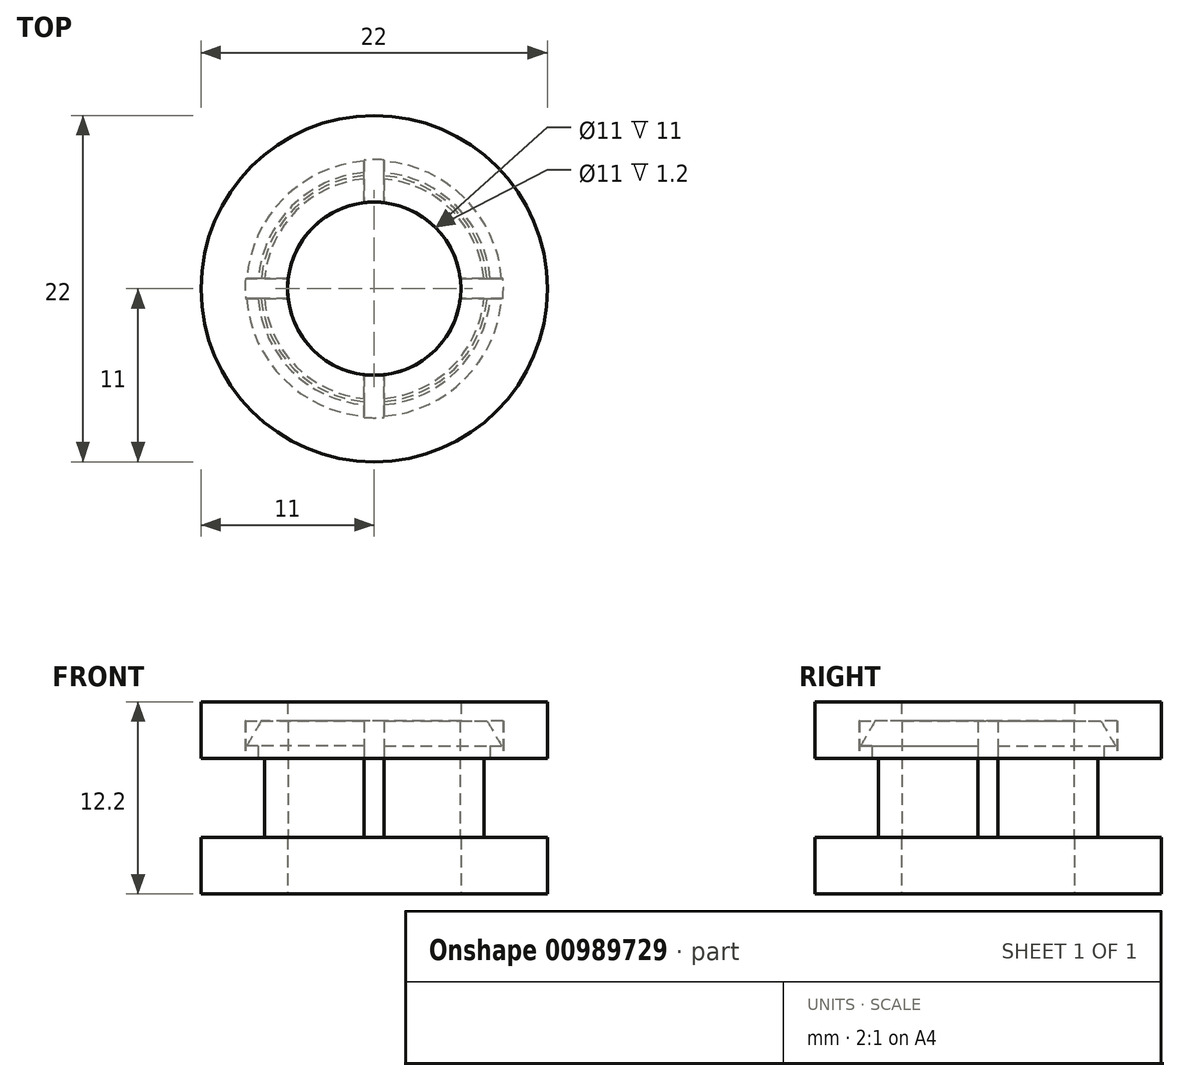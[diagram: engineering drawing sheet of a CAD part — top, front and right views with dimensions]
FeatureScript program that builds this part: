
annotation { "Feature Type Name" : "Feature", "Feature Type Description" : "" }
export const myFeature = defineFeature(function(context is Context, id is Id, definition is map)
    precondition{}
    {
        {
            assignVariable(context, id + "F0", {"name" : "WallThickness", "anyValue" : 5 * mm});
        }
        {
            assignVariable(context, id + "F1", {"name" : "WedgeLength", "anyValue" : 1.6 * mm});
        }
        {
            assignVariable(context, id + "F2", {"name" : "FlangeLength", "anyValue" : 0.8 * mm});
        }
        {
            assignVariable(context, id + "F3", {"name" : "CapThickness", "anyValue" : (getVariable(context, 'WedgeLength') + getVariable(context, 'FlangeLength')) + 1.2 * mm});
        }
        {
            var Q0;
            Q0=qCreatedBy(makeId("Top.planeOp"),FACE);
            var sketch = newSketch(context, id + "F4", { "sketchPlane" : qUnion([Q0])});
            skCircle(sketch, "E0", {"center": v(0, 0) * mm, "radius": 5.5 * mm});
            skCircle(sketch, "E1", {"center": v(0, 0) * mm, "radius": 7 * mm});
            skCircle(sketch, "E2", {"center": v(0, 0) * mm, "radius": 11 * mm});
            skCircle(sketch, "E3", {"center": v(0, 0) * mm, "radius": 8.2 * mm});
            skCircle(sketch, "E4", {"center": v(0, 0) * mm, "radius": 7.4 * mm});
            skLineSegment(sketch, "E5", {"start": v(0.64, -13.57) * mm, "end": v(0.64, 0) * mm});
            skLineSegment(sketch, "E6.MirrorCS", {"start": v(-0.64, -13.57) * mm, "end": v(-0.64, 0) * mm});
            skSolve(sketch);
        }
        {
            var Q0;
            Q0=qCreatedBy(makeId("Front.planeOp"),FACE);
            var sketch = newSketch(context, id + "F5", { "sketchPlane" : qUnion([Q0])});
            skLineSegment(sketch, "E7", {"start": v(0, 0) * mm, "end": v(0, 32.73) * mm, "construction": true});
            skSolve(sketch);
        }
        {
            var Q0;
            Q0=makeQuery(id+"F4.imprint","IMPRINT",FACE,{"disambiguationData":[TD([[makeQuery(id+"F4.imprint","IMPRINT",EDGE,{"derivedFrom":sQuery(id+"F4.wireOp",EDGE,"E2")}),1.0]])]});
            var Q1;
            Q1=makeQuery(id+"F4.imprint","IMPRINT",FACE,{"disambiguationData":[TD([[makeQuery(id+"F4.imprint","IMPRINT",EDGE,{"derivedFrom":sQuery(id+"F4.wireOp",EDGE,"E1")}),-1.0]])]});
            var Q2;
            Q2=makeQuery(id+"F4.imprint","IMPRINT",FACE,{"disambiguationData":[TD([[makeQuery(id+"F4.imprint","IMPRINT",EDGE,{"derivedFrom":sQuery(id+"F4.wireOp",EDGE,"E3")}),1.0]])]});
            extrude(context, id + "F6", {"entities" : qUnion([Q0, Q1, Q2]), "oppositeDirection" : true, "depth" : getVariable(context, 'CapThickness'), "offsetDistance" : 25 * mm});
        }
        {
            var Q0;
            Q0=makeQuery(id+"F4.imprint","IMPRINT",FACE,{"disambiguationData":[TD([[makeQuery(id+"F4.imprint","IMPRINT",EDGE,{"derivedFrom":sQuery(id+"F4.wireOp",EDGE,"E0")}),-1.0]])]});
            var Q1;
            Q1=makeQuery(id+"F4.imprint","IMPRINT",FACE,{"disambiguationData":[TD([[makeQuery(id+"F4.imprint","IMPRINT",EDGE,{"derivedFrom":sQuery(id+"F4.wireOp",EDGE,"E1")}),-1.0]])]});
            var Q2;
            Q2=makeQuery(id+"F4.imprint","IMPRINT",FACE,{"disambiguationData":[TD([[makeQuery(id+"F4.imprint","IMPRINT",EDGE,{"derivedFrom":sQuery(id+"F4.wireOp",EDGE,"E3")}),1.0]])]});
            extrude(context, id + "F7", {"entities" : qUnion([Q0, Q1, Q2]), "depth" : getVariable(context, 'WallThickness') + getVariable(context, 'WedgeLength') + getVariable(context, 'FlangeLength'), "offsetDistance" : 25 * mm});
        }
        {
            var Q0;
            Q0=makeQuery(id+"F4.imprint","IMPRINT",FACE,{"disambiguationData":[TD([[makeQuery(id+"F4.imprint","IMPRINT",EDGE,{"derivedFrom":sQuery(id+"F4.wireOp",EDGE,"E0")}),-1.0]])]});
            extrude(context, id + "F8", {"entities" : qUnion([Q0]), "operationType" : NewBodyOperationType.ADD, "oppositeDirection" : true, "depth" : getVariable(context, 'CapThickness'), "offsetDistance" : 25 * mm});
        }
        {
            var Q0;
            Q0=makeQuery(id+"F4.imprint","IMPRINT",FACE,{"disambiguationData":[TD([[makeQuery(id+"F4.imprint","IMPRINT",EDGE,{"derivedFrom":sQuery(id+"F4.wireOp",EDGE,"E3")}),1.0]])]});
            var Q1;
            Q1=makeQuery(id+"F4.imprint","IMPRINT",FACE,{"disambiguationData":[TD([[makeQuery(id+"F4.imprint","IMPRINT",EDGE,{"derivedFrom":sQuery(id+"F4.wireOp",EDGE,"E1")}),-1.0]])]});
            extrude(context, id + "F9", {"entities" : qUnion([Q0, Q1]), "operationType" : NewBodyOperationType.REMOVE, "depth" : getVariable(context, 'WallThickness'), "offsetDistance" : 25 * mm});
        }
        {
            var Q0;
            Q0=makeQuery(id+"F4.imprint","IMPRINT",FACE,{"disambiguationData":[TD([[makeQuery(id+"F4.imprint","IMPRINT",EDGE,{"derivedFrom":sQuery(id+"F4.wireOp",EDGE,"E3")}),1.0]])]});
            extrude(context, id + "F10", {"entities" : qUnion([Q0]), "operationType" : NewBodyOperationType.REMOVE, "depth" : getVariable(context, 'WallThickness') + getVariable(context, 'FlangeLength'), "offsetDistance" : 25 * mm});
        }
        {
            var Q0;
            Q0=makeQuery(id+"F7.opExtrude","CAP_EDGE",EDGE,{"disambiguationData":[OSD([sQuery(id+"F4.wireOp",EDGE,"E3")])],"isStart":false});
            chamfer(context, id + "F11", {"entities" : qUnion([Q0]), "chamferType" : ChamferType.OFFSET_ANGLE, "width" : 1 * mm, "oppositeDirection" : false, "angle" : 60 * degree});
        }
        {
            var Q0;
            {var subQ0=sQuery(id+"F4.wireOp",EDGE,"E5");var subQ1=sQuery(id+"F4.wireOp",EDGE,"E1");var subQ2=makeQuery(id+"F4.imprint","INTERSECT",VERTEX,{"derivedFrom":[subQ1,subQ0]});Q0=makeQuery(id+"F4.imprint","IMPRINT",FACE,{"disambiguationData":[TD([[makeQuery(id+"F4.imprint","IMPRINT",EDGE,{"disambiguationData":[TD([[subQ2,1.0]])],"derivedFrom":subQ1}),-1.0]])]});}
            var Q1;
            {var subQ0=sQuery(id+"F4.wireOp",EDGE,"E5");var subQ1=sQuery(id+"F4.wireOp",EDGE,"E3");var subQ2=makeQuery(id+"F4.imprint","INTERSECT",VERTEX,{"derivedFrom":[subQ1,subQ0]});Q1=makeQuery(id+"F4.imprint","IMPRINT",FACE,{"disambiguationData":[TD([[makeQuery(id+"F4.imprint","IMPRINT",EDGE,{"disambiguationData":[TD([[subQ2,1.0]])],"derivedFrom":subQ1}),1.0]])]});}
            var Q2;
            {var subQ0=sQuery(id+"F4.wireOp",EDGE,"E5");var subQ1=sQuery(id+"F4.wireOp",EDGE,"E2");var subQ2=makeQuery(id+"F4.imprint","INTERSECT",VERTEX,{"derivedFrom":[subQ1,subQ0]});Q2=makeQuery(id+"F4.imprint","IMPRINT",FACE,{"disambiguationData":[TD([[makeQuery(id+"F4.imprint","IMPRINT",EDGE,{"disambiguationData":[TD([[subQ2,1.0]])],"derivedFrom":subQ1}),1.0]])]});}
            var Q3;
            {var subQ0=sQuery(id+"F4.wireOp",EDGE,"E5");var subQ1=sQuery(id+"F4.wireOp",EDGE,"E0");var subQ2=makeQuery(id+"F4.imprint","INTERSECT",VERTEX,{"derivedFrom":[subQ1,subQ0]});Q3=makeQuery(id+"F4.imprint","IMPRINT",FACE,{"disambiguationData":[TD([[makeQuery(id+"F4.imprint","IMPRINT",EDGE,{"disambiguationData":[TD([[subQ2,1.0]])],"derivedFrom":subQ1}),-1.0]])]});}
            extrude(context, id + "F12", {"entities" : qUnion([Q0, Q1, Q2, Q3]), "depth" : 25 * mm, "offsetDistance" : 25 * mm});
        }
        {
            var Q0;
            Q0=makeQuery(id+"F12.opExtrude","SWEPT_BODY",BODY,{"disambiguationData":[OSD([sQuery(id+"F4.wireOp",EDGE,"E0"),sQuery(id+"F4.wireOp",EDGE,"E2"),sQuery(id+"F4.wireOp",EDGE,"E5"),sQuery(id+"F4.wireOp",EDGE,"E6.MirrorCS")])]});
            var Q1;
            Q1=sQuery(id+"F5.wireOp",EDGE,"E7");
            circularPattern(context, id + "F13", {"operationType" : NewBodyOperationType.REMOVE, "entities" : qUnion([Q0]), "axis" : qUnion([Q1]), "angle" : 360 * degree, "instanceCount" : 4, "equalSpace" : true});
        }
        {
            var Q0;
            {var subQ0=sQuery(id+"F4.wireOp",EDGE,"E5");var subQ1=sQuery(id+"F4.wireOp",EDGE,"E2");var subQ2=makeQuery(id+"F4.imprint","INTERSECT",VERTEX,{"derivedFrom":[subQ1,subQ0]});Q0=makeQuery(id+"F4.imprint","IMPRINT",FACE,{"disambiguationData":[TD([[makeQuery(id+"F4.imprint","IMPRINT",EDGE,{"disambiguationData":[TD([[subQ2,-1.0]])],"derivedFrom":subQ1}),1.0]])]});}
            var Q1;
            {var subQ0=sQuery(id+"F4.wireOp",EDGE,"E5");var subQ1=sQuery(id+"F4.wireOp",EDGE,"E3");var subQ2=makeQuery(id+"F4.imprint","INTERSECT",VERTEX,{"derivedFrom":[subQ1,subQ0]});Q1=makeQuery(id+"F4.imprint","IMPRINT",FACE,{"disambiguationData":[TD([[makeQuery(id+"F4.imprint","IMPRINT",EDGE,{"disambiguationData":[TD([[subQ2,-1.0]])],"derivedFrom":subQ1}),1.0]])]});}
            var Q2;
            {var subQ0=sQuery(id+"F4.wireOp",EDGE,"E5");var subQ1=sQuery(id+"F4.wireOp",EDGE,"E2");var subQ2=makeQuery(id+"F4.imprint","INTERSECT",VERTEX,{"derivedFrom":[subQ1,subQ0]});Q2=makeQuery(id+"F4.imprint","IMPRINT",FACE,{"disambiguationData":[TD([[makeQuery(id+"F4.imprint","IMPRINT",EDGE,{"disambiguationData":[TD([[subQ2,1.0]])],"derivedFrom":subQ1}),1.0]])]});}
            var Q3;
            {var subQ0=sQuery(id+"F4.wireOp",EDGE,"E5");var subQ1=sQuery(id+"F4.wireOp",EDGE,"E3");var subQ2=makeQuery(id+"F4.imprint","INTERSECT",VERTEX,{"derivedFrom":[subQ1,subQ0]});Q3=makeQuery(id+"F4.imprint","IMPRINT",FACE,{"disambiguationData":[TD([[makeQuery(id+"F4.imprint","IMPRINT",EDGE,{"disambiguationData":[TD([[subQ2,1.0]])],"derivedFrom":subQ1}),1.0]])]});}
            var Q4;
            {var subQ0=sQuery(id+"F4.wireOp",EDGE,"E5");var subQ1=sQuery(id+"F4.wireOp",EDGE,"E1");var subQ2=makeQuery(id+"F4.imprint","INTERSECT",VERTEX,{"derivedFrom":[subQ1,subQ0]});Q4=makeQuery(id+"F4.imprint","IMPRINT",FACE,{"disambiguationData":[TD([[makeQuery(id+"F4.imprint","IMPRINT",EDGE,{"disambiguationData":[TD([[subQ2,1.0]])],"derivedFrom":subQ1}),-1.0]])]});}
            var Q5;
            {var subQ0=sQuery(id+"F4.wireOp",EDGE,"E5");var subQ1=sQuery(id+"F4.wireOp",EDGE,"E1");var subQ2=makeQuery(id+"F4.imprint","INTERSECT",VERTEX,{"derivedFrom":[subQ1,subQ0]});Q5=makeQuery(id+"F4.imprint","IMPRINT",FACE,{"disambiguationData":[TD([[makeQuery(id+"F4.imprint","IMPRINT",EDGE,{"disambiguationData":[TD([[subQ2,-1.0]])],"derivedFrom":subQ1}),-1.0]])]});}
            var Q6;
            {var subQ0=sQuery(id+"F4.wireOp",EDGE,"E5");var subQ1=sQuery(id+"F4.wireOp",EDGE,"E0");var subQ2=makeQuery(id+"F4.imprint","INTERSECT",VERTEX,{"derivedFrom":[subQ1,subQ0]});Q6=makeQuery(id+"F4.imprint","IMPRINT",FACE,{"disambiguationData":[TD([[makeQuery(id+"F4.imprint","IMPRINT",EDGE,{"disambiguationData":[TD([[subQ2,-1.0]])],"derivedFrom":subQ1}),-1.0]])]});}
            var Q7;
            {var subQ0=sQuery(id+"F4.wireOp",EDGE,"E5");var subQ1=sQuery(id+"F4.wireOp",EDGE,"E0");var subQ2=makeQuery(id+"F4.imprint","INTERSECT",VERTEX,{"derivedFrom":[subQ1,subQ0]});Q7=makeQuery(id+"F4.imprint","IMPRINT",FACE,{"disambiguationData":[TD([[makeQuery(id+"F4.imprint","IMPRINT",EDGE,{"disambiguationData":[TD([[subQ2,1.0]])],"derivedFrom":subQ1}),-1.0]])]});}
            extrude(context, id + "F14", {"entities" : qUnion([Q0, Q1, Q2, Q3, Q4, Q5, Q6, Q7]), "depth" : getVariable(context, 'CapThickness') + getVariable(context, 'WallThickness'), "offsetDistance" : 25 * mm, "hasSecondDirection" : true, "secondDirectionOppositeDirection" : false, "secondDirectionDepth" : getVariable(context, 'WallThickness')});
        }
        {
            var Q0;
            {var subQ0=sQuery(id+"F4.wireOp",EDGE,"E5");var subQ1=sQuery(id+"F4.wireOp",EDGE,"E0");var subQ2=makeQuery(id+"F4.imprint","INTERSECT",VERTEX,{"derivedFrom":[subQ1,subQ0]});Q0=makeQuery(id+"F4.imprint","IMPRINT",FACE,{"disambiguationData":[TD([[makeQuery(id+"F4.imprint","IMPRINT",EDGE,{"disambiguationData":[TD([[subQ2,1.0]])],"derivedFrom":subQ1}),-1.0]])]});}
            var Q1;
            {var subQ0=sQuery(id+"F4.wireOp",EDGE,"E5");var subQ1=sQuery(id+"F4.wireOp",EDGE,"E1");var subQ2=makeQuery(id+"F4.imprint","INTERSECT",VERTEX,{"derivedFrom":[subQ1,subQ0]});Q1=makeQuery(id+"F4.imprint","IMPRINT",FACE,{"disambiguationData":[TD([[makeQuery(id+"F4.imprint","IMPRINT",EDGE,{"disambiguationData":[TD([[subQ2,1.0]])],"derivedFrom":subQ1}),-1.0]])]});}
            var Q2;
            {var subQ0=sQuery(id+"F4.wireOp",EDGE,"E5");var subQ1=sQuery(id+"F4.wireOp",EDGE,"E3");var subQ2=makeQuery(id+"F4.imprint","INTERSECT",VERTEX,{"derivedFrom":[subQ1,subQ0]});Q2=makeQuery(id+"F4.imprint","IMPRINT",FACE,{"disambiguationData":[TD([[makeQuery(id+"F4.imprint","IMPRINT",EDGE,{"disambiguationData":[TD([[subQ2,1.0]])],"derivedFrom":subQ1}),1.0]])]});}
            extrude(context, id + "F15", {"entities" : qUnion([Q0, Q1, Q2]), "depth" : getVariable(context, 'WallThickness') + getVariable(context, 'FlangeLength') + getVariable(context, 'WedgeLength'), "offsetDistance" : 25 * mm, "hasSecondDirection" : true, "secondDirectionOppositeDirection" : false, "secondDirectionDepth" : getVariable(context, 'WallThickness')});
        }
        {
            var Q0;
            Q0=makeQuery(id+"F15.opExtrude","SWEPT_BODY",BODY,{"disambiguationData":[OSD([sQuery(id+"F4.wireOp",EDGE,"E0"),sQuery(id+"F4.wireOp",EDGE,"E4"),sQuery(id+"F4.wireOp",EDGE,"E5"),sQuery(id+"F4.wireOp",EDGE,"E6.MirrorCS")])]});
            var Q1;
            Q1=sQuery(id+"F5.wireOp",EDGE,"E7");
            circularPattern(context, id + "F16", {"operationType" : NewBodyOperationType.REMOVE, "entities" : qUnion([Q0]), "axis" : qUnion([Q1]), "angle" : 360 * degree, "instanceCount" : 4, "equalSpace" : true});
        }
        {
            var Q0;
            Q0=makeQuery(id+"F6.opExtrude","SWEPT_BODY",BODY,{"disambiguationData":[OSD([sQuery(id+"F4.wireOp",EDGE,"E1"),sQuery(id+"F4.wireOp",EDGE,"E2")])]});
            var Q1;
            Q1=makeQuery(id+"F14.opExtrude","SWEPT_BODY",BODY,{"disambiguationData":[OSD([sQuery(id+"F4.wireOp",EDGE,"E2")])]});
            booleanBodies(context, id + "F17", {"operationType" : BooleanOperationType.SUBTRACTION, "tools" : qUnion([Q0]), "targets" : qUnion([Q1]), "keepTools" : true});
        }
    });
